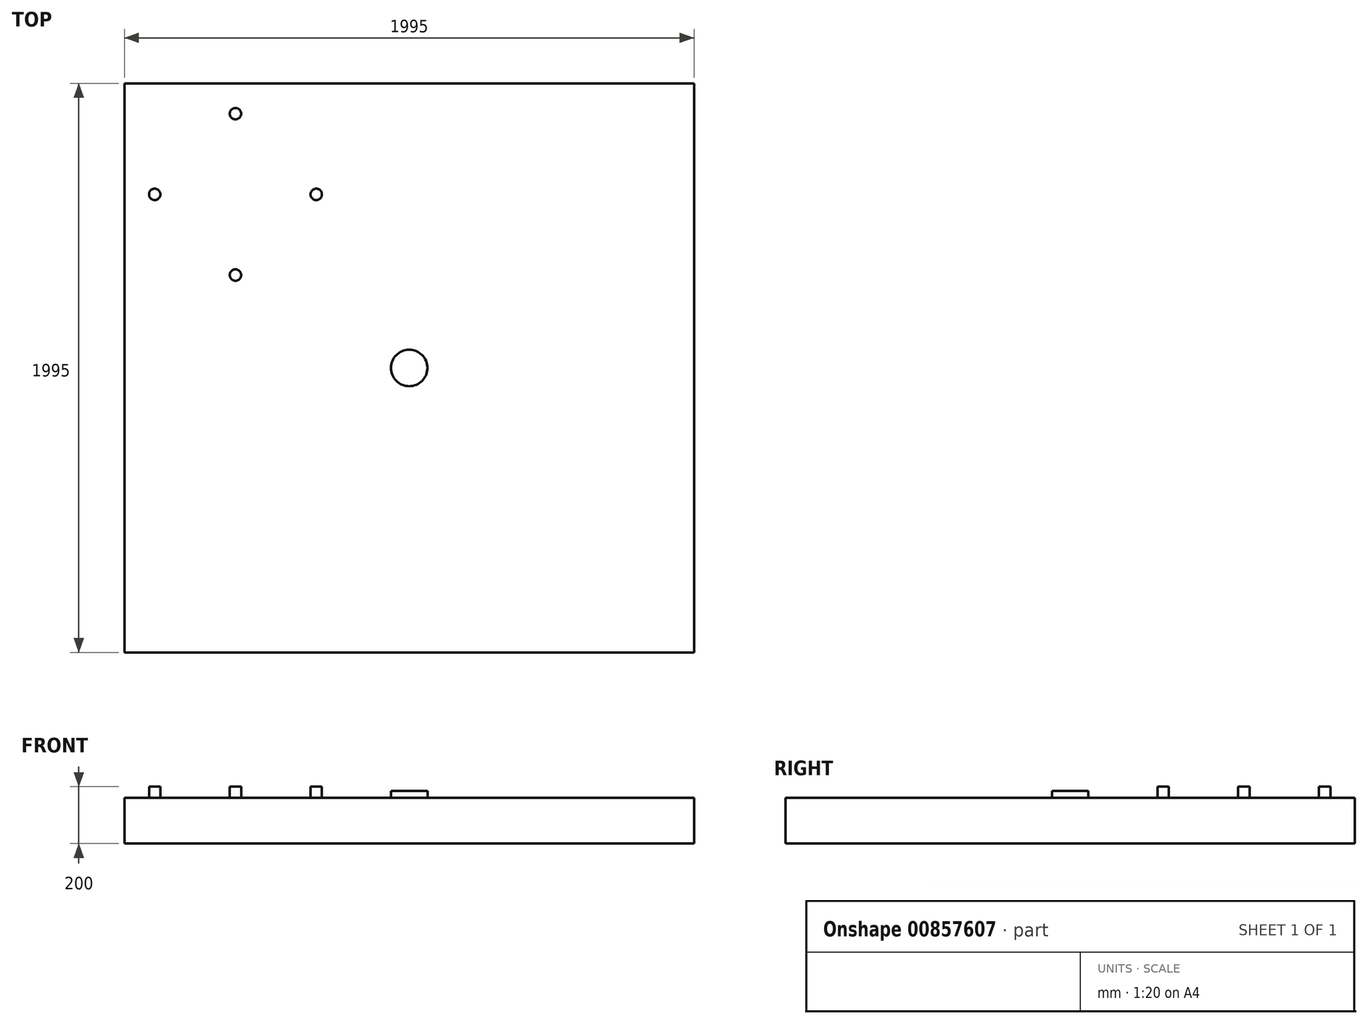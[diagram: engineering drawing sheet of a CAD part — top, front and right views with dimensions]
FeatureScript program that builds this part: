
annotation { "Feature Type Name" : "Feature", "Feature Type Description" : "" }
export const myFeature = defineFeature(function(context is Context, id is Id, definition is map)
    precondition{}
    {
        {
            var Q0;
            Q0=qCreatedBy(makeId("Top.planeOp"),FACE);
            var sketch = newSketch(context, id + "F0", { "sketchPlane" : qUnion([Q0])});
            skLineSegment(sketch, "E0.bottom", {"start": v(997.5, 997.5) * mm, "end": v(-997.5, 997.5) * mm});
            skLineSegment(sketch, "E0.top", {"start": v(997.5, -997.5) * mm, "end": v(-997.5, -997.5) * mm});
            skLineSegment(sketch, "E0.left", {"start": v(997.5, 997.5) * mm, "end": v(997.5, -997.5) * mm});
            skLineSegment(sketch, "E0.right", {"start": v(-997.5, 997.5) * mm, "end": v(-997.5, -997.5) * mm});
            skPoint(sketch, "E0.middle", {"position": v(0, 0) * mm});
            skSolve(sketch);
        }
        {
            var Q0;
            Q0 = qSketchRegion(id + "F0", true);
            extrude(context, id + "F1", {"entities" : qUnion([Q0]), "depth" : 160 * mm, "offsetDistance" : 25 * mm});
        }
        {
            var Q0;
            Q0=makeQuery(id+"F1.opExtrude","CAP_FACE",FACE,{"disambiguationData":[OSD([sQuery(id+"F0.wireOp",EDGE,"E0.bottom"),sQuery(id+"F0.wireOp",EDGE,"E0.top"),sQuery(id+"F0.wireOp",EDGE,"E0.left"),sQuery(id+"F0.wireOp",EDGE,"E0.right")])],"isStart":false});
            var sketch = newSketch(context, id + "F2", { "sketchPlane" : qUnion([Q0])});
            skLineSegment(sketch, "E1", {"start": v(-997.5, 997.5) * mm, "end": v(0, 0) * mm, "construction": true});
            skLineSegment(sketch, "E2", {"start": v(0, 0) * mm, "end": v(997.5, 997.5) * mm, "construction": true});
            skLineSegment(sketch, "E3", {"start": v(0, 0) * mm, "end": v(-997.5, -997.5) * mm, "construction": true});
            skLineSegment(sketch, "E4", {"start": v(0, 0) * mm, "end": v(997.5, -997.5) * mm, "construction": true});
            skLineSegment(sketch, "E5", {"start": v(-891.43, 608.6) * mm, "end": v(-608.6, 891.43) * mm, "construction": true});
            skLineSegment(sketch, "E6", {"start": v(-608.6, 891.43) * mm, "end": v(-325.75, 608.6) * mm, "construction": true});
            skLineSegment(sketch, "E7", {"start": v(-325.75, 608.6) * mm, "end": v(-608.6, 325.75) * mm, "construction": true});
            skLineSegment(sketch, "E8", {"start": v(-608.6, 325.75) * mm, "end": v(-891.43, 608.6) * mm, "construction": true});
            skCircle(sketch, "E9", {"center": v(-608.6, 891.43) * mm, "radius": 20 * mm});
            skCircle(sketch, "E10", {"center": v(-325.75, 608.6) * mm, "radius": 20 * mm});
            skCircle(sketch, "E11", {"center": v(-608.6, 325.75) * mm, "radius": 20 * mm});
            skCircle(sketch, "E12", {"center": v(-891.43, 608.6) * mm, "radius": 20 * mm});
            skSolve(sketch);
        }
        {
            var Q0;
            Q0 = qSketchRegion(id + "F2", true);
            extrude(context, id + "F3", {"entities" : qUnion([Q0]), "operationType" : NewBodyOperationType.ADD, "depth" : 40 * mm, "offsetDistance" : 25 * mm});
        }
        {
            var Q0;
            Q0=makeQuery(id+"F1.opExtrude","CAP_FACE",FACE,{"disambiguationData":[OSD([sQuery(id+"F0.wireOp",EDGE,"E0.bottom"),sQuery(id+"F0.wireOp",EDGE,"E0.top"),sQuery(id+"F0.wireOp",EDGE,"E0.left"),sQuery(id+"F0.wireOp",EDGE,"E0.right")])],"isStart":false});
            var sketch = newSketch(context, id + "F4", { "sketchPlane" : qUnion([Q0])});
            skCircle(sketch, "E13", {"center": v(0, 0) * mm, "radius": 63.88 * mm});
            skSolve(sketch);
        }
        {
            var Q0;
            Q0 = qSketchRegion(id + "F4", true);
            extrude(context, id + "F5", {"entities" : qUnion([Q0]), "operationType" : NewBodyOperationType.ADD, "depth" : 25 * mm, "offsetDistance" : 25 * mm});
        }
    });
